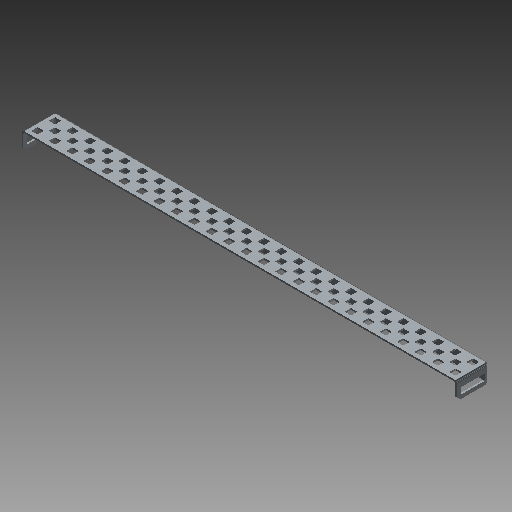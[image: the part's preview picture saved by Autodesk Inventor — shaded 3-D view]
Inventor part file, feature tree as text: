
AUTODESK INVENTOR PART (.ipt)
format: ipt  version: 2018 (Build 220112000, 112)  size: 1,924,608 bytes
history: native  units: mm (DEFAULTED — no unit token found)
features: other x103, extrude x103, sketch x4, pattern_linear x3, imported_body x1
ambient origin geometry x8: Origin, YZ Plane, XZ Plane, XY Plane, X Axis, Y Axis, Z Axis, Center Point
bodies: Solid1 (feature_tree)
feature tree (214):
  imported_body  "Base1"
  sketch  "Sketch1"  dims[d2=1.1684mm]
  pattern_linear  "Rectangular Pattern1"  Count1=25  [1 undecoded]
  pattern_linear  "Rectangular Pattern2"  Spacing1=12.7mm  [1 undecoded]
  sketch  "Sketch2"  dims[d3=0.0mm]
  sketch  "Sketch3"  dims[d4=1.1684mm]
  pattern_linear  "Rectangular Pattern3"  Count1=2 Spacing1=12.7mm
  other  "Srf1"
  other  "Srf2"
  other  "Srf3"
  other  "Srf4"
  other  "Srf5"
  other  "Srf6"
  other  "Srf7"
  other  "Srf8"
  other  "Srf9"
  other  "Srf10"
  other  "Srf11"
  other  "Srf12"
  other  "Srf13"
  other  "Srf14"
  other  "Srf15"
  other  "Srf16"
  other  "Srf17"
  other  "Srf18"
  other  "Srf19"
  other  "Srf20"
  other  "Srf21"
  other  "Srf22"
  other  "Srf23"
  other  "Srf24"
  other  "Srf25"
  other  "Srf26"
  other  "Srf27"
  other  "Srf28"
  other  "Srf29"
  other  "Srf30"
  other  "Srf31"
  other  "Srf32"
  other  "Srf33"
  other  "Srf34"
  other  "Srf35"
  other  "Srf36"
  other  "Srf37"
  other  "Srf38"
  other  "Srf39"
  other  "Srf40"
  other  "Srf41"
  other  "Srf42"
  other  "Srf43"
  other  "Srf44"
  other  "Srf45"
  other  "Srf46"
  other  "Srf47"
  other  "Srf48"
  other  "Srf49"
  other  "Srf50"
  other  "Srf51"
  other  "Srf52"
  other  "Srf53"
  other  "Srf54"
  other  "Srf55"
  other  "Srf56"
  other  "Srf57"
  other  "Srf58"
  other  "Srf59"
  other  "Srf60"
  other  "Srf61"
  other  "Srf62"
  other  "Srf63"
  other  "Srf64"
  other  "Srf65"
  other  "Srf66"
  other  "Srf67"
  other  "Srf68"
  other  "Srf69"
  other  "Srf70"
  other  "Srf71"
  other  "Srf72"
  other  "Srf73"
  other  "Srf74"
  other  "Srf75"
  other  "Srf76"
  other  "Srf77"
  other  "Srf78"
  sketch  "Sketch4"  dims[d5=0.0mm d6=250.0mm d8=12.7mm d9=20.0mm d11=12.7mm d12=240.0mm d14=12.7mm d15=1.1684mm d16=0.0mm d17=1.1684mm d18=0.0mm d19=1.1684mm d20=0.0mm d21=1.1684mm d22=0.0mm d23=1.1684mm d24=0.0mm d25=250.0mm d27=12.7mm d28=0.0mm d29=0.0mm d30=0.0mm d31=0.0mm d32=0.0mm d33=0.0mm d34=0.0mm d35=0.0mm d36=0.0mm d37=0.0mm d38=0.0mm d39=0.0mm d40=0.0mm d41=0.0mm d42=0.0mm d43=0.0mm d44=0.0mm d45=0.0mm d46=0.0mm d47=0.0mm d48=0.0mm d49=0.0mm d50=0.0mm d51=0.0mm d52=0.0mm d53=0.0mm d54=0.0mm d55=0.0mm d56=0.0mm d57=0.0mm d58=0.0mm d59=0.0mm d60=0.0mm d61=0.0mm d62=0.0mm d63=0.0mm d64=0.0mm d65=0.0mm d66=0.0mm d67=0.0mm d68=0.0mm d69=0.0mm d70=0.0mm d71=0.0mm d72=0.0mm d73=0.0mm d74=0.0mm d75=0.0mm d76=0.0mm d77=0.0mm d78=0.0mm d79=0.0mm d80=0.0mm d81=0.0mm d82=0.0mm d83=0.0mm d84=0.0mm d85=0.0mm d86=0.0mm d87=0.0mm d88=0.0mm d89=0.0mm d90=0.0mm d91=0.0mm d92=0.0mm d93=0.0mm d94=0.0mm d95=0.0mm d96=0.0mm d97=0.0mm d98=0.0mm d99=0.0mm d100=0.0mm d101=0.0mm d102=0.0mm d103=0.0mm d104=0.0mm d105=0.0mm d106=0.0mm d107=0.0mm d108=0.0mm d109=0.0mm d110=0.0mm d111=0.0mm d112=0.0mm d113=0.0mm d114=0.0mm d115=0.0mm d116=0.0mm d117=0.0mm d118=0.0mm d119=0.0mm d120=0.0mm d121=0.0mm d122=0.0mm d123=0.0mm d124=0.0mm d125=0.0mm d126=0.0mm d127=0.0mm d128=0.0mm d129=0.0mm d130=0.0mm d131=0.0mm d132=0.0mm d133=0.0mm d134=0.0mm d135=0.0mm d136=0.0mm d137=0.0mm d138=0.0mm d139=0.0mm d140=0.0mm d141=0.0mm d142=0.0mm d143=0.0mm d144=0.0mm d145=0.0mm d146=0.0mm d147=0.0mm d148=0.0mm d149=0.0mm d150=0.0mm d151=0.0mm d152=0.0mm d153=0.0mm d154=0.0mm d155=0.0mm d156=0.0mm d157=0.0mm d158=0.0mm d159=0.0mm d160=0.0mm d161=0.0mm d162=0.0mm d163=0.0mm d164=0.0mm d165=0.0mm d166=0.0mm d167=0.0mm d168=0.0mm d169=0.0mm d170=0.0mm d171=0.0mm d172=0.0mm d173=0.0mm d174=0.0mm d175=0.0mm d176=0.0mm d177=0.0mm d178=0.0mm d179=0.0mm d180=0.0mm d181=0.0mm d182=0.0mm d183=0.0mm d184=0.0mm d185=0.0mm d186=0.0mm d187=0.0mm d188=0.0mm d189=0.0mm d190=0.0mm d191=0.0mm d192=0.0mm d193=0.0mm d194=0.0mm d195=0.0mm d196=0.0mm d197=0.0mm d198=0.0mm d199=0.0mm d200=0.0mm d201=0.0mm d202=0.0mm d203=0.0mm d204=0.0mm d205=0.0mm d206=0.0mm d207=0.0mm d208=0.0mm d209=0.0mm d210=0.0mm d211=0.0mm d212=0.0mm d213=0.0mm d214=0.0mm d215=0.0mm d216=0.0mm d217=0.0mm d218=0.0mm d219=0.0mm d220=0.0mm d221=0.0mm d222=0.0mm d223=0.0mm d224=0.0mm d225=0.0mm d226=0.0mm d227=0.0mm d228=0.0mm d229=0.0mm d230=0.0mm d231=0.0mm d232=0.0mm d233=0.0mm]
  other  "Srf79"
  other  "Srf80"
  other  "Srf81"
  other  "Srf82"
  other  "Srf83"
  other  "Srf84"
  other  "Srf85"
  other  "Srf86"
  other  "Srf87"
  other  "Srf88"
  other  "Srf89"
  other  "Srf90"
  other  "Srf91"
  other  "Srf92"
  other  "Srf93"
  other  "Srf94"
  other  "Srf95"
  other  "Srf96"
  other  "Srf97"
  other  "Srf98"
  other  "Srf99"
  other  "Srf100"
  other  "Srf101"
  other  "Srf102"
  other  "Srf103"
  extrude  "ExtrusionSrf1"  Depth=240.0mm
  extrude  "ExtrusionSrf2"  Depth=12.7mm
  extrude  "ExtrusionSrf75"  Depth=1.1684mm
  extrude  "ExtrusionSrf76"  TaperAngle=0.0deg  [1 undecoded]
  extrude  "ExtrusionSrf77"  Depth=1.1684mm
  extrude  "ExtrusionSrf78"  TaperAngle=0.0deg  [1 undecoded]
  extrude  "ExtrusionSrf79"  Depth=1.1684mm
  extrude  "ExtrusionSrf3"  TaperAngle=0.0deg  [1 undecoded]
  extrude  "ExtrusionSrf4"  Depth=1.1684mm
  extrude  "ExtrusionSrf5"  TaperAngle=0.0deg  [1 undecoded]
  extrude  "ExtrusionSrf6"  Depth=1.1684mm
  extrude  "ExtrusionSrf7"  TaperAngle=0.0deg  [1 undecoded]
  extrude  "ExtrusionSrf8"  Depth=250.0mm
  extrude  "ExtrusionSrf9"  Depth=12.7mm
  extrude  "ExtrusionSrf10"  [1 undecoded]
  extrude  "ExtrusionSrf11"  [1 undecoded]
  extrude  "ExtrusionSrf12"  [1 undecoded]
  extrude  "ExtrusionSrf13"  [1 undecoded]
  extrude  "ExtrusionSrf14"  [1 undecoded]
  extrude  "ExtrusionSrf15"  [1 undecoded]
  extrude  "ExtrusionSrf16"  [1 undecoded]
  extrude  "ExtrusionSrf17"  [1 undecoded]
  extrude  "ExtrusionSrf18"  [1 undecoded]
  extrude  "ExtrusionSrf19"  [1 undecoded]
  extrude  "ExtrusionSrf20"  [1 undecoded]
  extrude  "ExtrusionSrf21"  [1 undecoded]
  extrude  "ExtrusionSrf22"  [1 undecoded]
  extrude  "ExtrusionSrf23"  [1 undecoded]
  extrude  "ExtrusionSrf24"  [1 undecoded]
  extrude  "ExtrusionSrf25"  [1 undecoded]
  extrude  "ExtrusionSrf26"  [1 undecoded]
  extrude  "ExtrusionSrf27"  [1 undecoded]
  extrude  "ExtrusionSrf28"  [1 undecoded]
  extrude  "ExtrusionSrf29"  [1 undecoded]
  extrude  "ExtrusionSrf30"  [1 undecoded]
  extrude  "ExtrusionSrf31"  [1 undecoded]
  extrude  "ExtrusionSrf32"  [1 undecoded]
  extrude  "ExtrusionSrf33"  [1 undecoded]
  extrude  "ExtrusionSrf34"  [1 undecoded]
  extrude  "ExtrusionSrf35"  [1 undecoded]
  extrude  "ExtrusionSrf36"  [1 undecoded]
  extrude  "ExtrusionSrf37"  [1 undecoded]
  extrude  "ExtrusionSrf38"  [1 undecoded]
  extrude  "ExtrusionSrf39"  [1 undecoded]
  extrude  "ExtrusionSrf40"  [1 undecoded]
  extrude  "ExtrusionSrf41"  [1 undecoded]
  extrude  "ExtrusionSrf42"  [1 undecoded]
  extrude  "ExtrusionSrf43"  [1 undecoded]
  extrude  "ExtrusionSrf44"  [1 undecoded]
  extrude  "ExtrusionSrf45"  [1 undecoded]
  extrude  "ExtrusionSrf46"  [1 undecoded]
  extrude  "ExtrusionSrf47"  [1 undecoded]
  extrude  "ExtrusionSrf48"  [1 undecoded]
  extrude  "ExtrusionSrf49"  [1 undecoded]
  extrude  "ExtrusionSrf50"  [1 undecoded]
  extrude  "ExtrusionSrf51"  [1 undecoded]
  extrude  "ExtrusionSrf52"  [1 undecoded]
  extrude  "ExtrusionSrf53"  [1 undecoded]
  extrude  "ExtrusionSrf54"  [1 undecoded]
  extrude  "ExtrusionSrf55"  [1 undecoded]
  extrude  "ExtrusionSrf56"  [1 undecoded]
  extrude  "ExtrusionSrf57"  [1 undecoded]
  extrude  "ExtrusionSrf58"  [1 undecoded]
  extrude  "ExtrusionSrf59"  [1 undecoded]
  extrude  "ExtrusionSrf60"  [1 undecoded]
  extrude  "ExtrusionSrf61"  [1 undecoded]
  extrude  "ExtrusionSrf62"  [1 undecoded]
  extrude  "ExtrusionSrf63"  [1 undecoded]
  extrude  "ExtrusionSrf64"  [1 undecoded]
  extrude  "ExtrusionSrf65"  [1 undecoded]
  extrude  "ExtrusionSrf66"  [1 undecoded]
  extrude  "ExtrusionSrf67"  [1 undecoded]
  extrude  "ExtrusionSrf68"  [1 undecoded]
  extrude  "ExtrusionSrf69"  [1 undecoded]
  extrude  "ExtrusionSrf70"  [1 undecoded]
  extrude  "ExtrusionSrf71"  [1 undecoded]
  extrude  "ExtrusionSrf72"  [1 undecoded]
  extrude  "ExtrusionSrf73"  [1 undecoded]
  extrude  "ExtrusionSrf74"  [1 undecoded]
  extrude  "ExtrusionSrf80"  [1 undecoded]
  extrude  "ExtrusionSrf81"  [1 undecoded]
  extrude  "ExtrusionSrf82"  [1 undecoded]
  extrude  "ExtrusionSrf83"  [1 undecoded]
  extrude  "ExtrusionSrf84"  [1 undecoded]
  extrude  "ExtrusionSrf85"  [1 undecoded]
  extrude  "ExtrusionSrf86"  [1 undecoded]
  extrude  "ExtrusionSrf87"  [1 undecoded]
  extrude  "ExtrusionSrf88"  [1 undecoded]
  extrude  "ExtrusionSrf89"  [1 undecoded]
  extrude  "ExtrusionSrf90"  [1 undecoded]
  extrude  "ExtrusionSrf91"  [1 undecoded]
  extrude  "ExtrusionSrf92"  [1 undecoded]
  extrude  "ExtrusionSrf93"  [1 undecoded]
  extrude  "ExtrusionSrf94"  [1 undecoded]
  extrude  "ExtrusionSrf95"  [1 undecoded]
  extrude  "ExtrusionSrf96"  [1 undecoded]
  extrude  "ExtrusionSrf97"  [1 undecoded]
  extrude  "ExtrusionSrf98"  [1 undecoded]
  extrude  "ExtrusionSrf99"  [1 undecoded]
  extrude  "ExtrusionSrf100"  [1 undecoded]
  extrude  "ExtrusionSrf101"  [1 undecoded]
  extrude  "ExtrusionSrf102"  [1 undecoded]
  extrude  "ExtrusionSrf103"  [1 undecoded]
note: 96 required parameter values undecoded (feature->parameter linkage not recoverable at this tier; creation-order binding heuristic only, values carry confidence <= 0.55)
